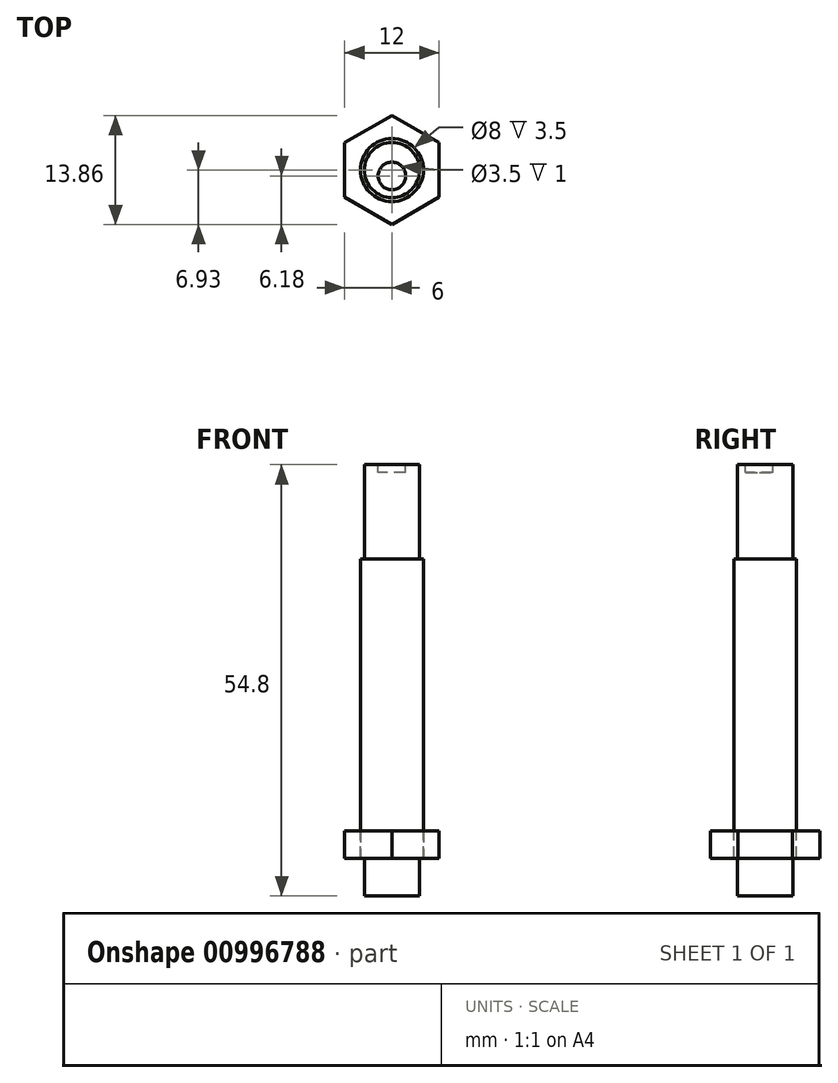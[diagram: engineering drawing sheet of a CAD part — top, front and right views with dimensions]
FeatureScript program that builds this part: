
annotation { "Feature Type Name" : "Feature", "Feature Type Description" : "" }
export const myFeature = defineFeature(function(context is Context, id is Id, definition is map)
    precondition{}
    {
        {
            var Q0;
            Q0=qCreatedBy(makeId("Front.planeOp"),FACE);
            var sketch = newSketch(context, id + "F0", { "sketchPlane" : qUnion([Q0])});
            skLineSegment(sketch, "E0.bottom", {"start": v(0, 0) * mm, "end": v(-4, 0) * mm});
            skLineSegment(sketch, "E0.top", {"start": v(0, 38) * mm, "end": v(-4, 38) * mm});
            skLineSegment(sketch, "E0.left", {"start": v(0, 0) * mm, "end": v(0, 38) * mm});
            skLineSegment(sketch, "E0.right", {"start": v(-4, 0) * mm, "end": v(-4, 38) * mm});
            skLineSegment(sketch, "E1.bottom", {"start": v(0, 0) * mm, "end": v(-3.5, 0) * mm});
            skLineSegment(sketch, "E1.top", {"start": v(0, -4.8) * mm, "end": v(-3.5, -4.8) * mm});
            skLineSegment(sketch, "E1.left", {"start": v(0, 0) * mm, "end": v(0, -4.8) * mm});
            skLineSegment(sketch, "E1.right", {"start": v(-3.5, 0) * mm, "end": v(-3.5, -4.8) * mm});
            skLineSegment(sketch, "E2.bottom", {"start": v(0, 38) * mm, "end": v(-3.5, 38) * mm});
            skLineSegment(sketch, "E2.top", {"start": v(0, 50) * mm, "end": v(-3.5, 50) * mm});
            skLineSegment(sketch, "E2.left", {"start": v(0, 38) * mm, "end": v(0, 50) * mm});
            skLineSegment(sketch, "E2.right", {"start": v(-3.5, 38) * mm, "end": v(-3.5, 50) * mm});
            skSolve(sketch);
        }
        {
            var Q0;
            {var subQ3=sQuery(id+"F0.wireOp",EDGE,"E0.left");Q0=makeQuery(id+"F0.imprint","IMPRINT",FACE,{"disambiguationData":[TD([[makeQuery(id+"F0.imprint","IMPRINT",EDGE,{"derivedFrom":subQ3}),1.0]])]});}
            var Q1;
            Q1=makeQuery(id+"F0.imprint","IMPRINT",FACE,{"disambiguationData":[TD([[makeQuery(id+"F0.imprint","IMPRINT",EDGE,{"derivedFrom":sQuery(id+"F0.wireOp",EDGE,"E1.top")}),-1.0]])]});
            var Q2;
            Q2=makeQuery(id+"F0.imprint","IMPRINT",FACE,{"disambiguationData":[TD([[makeQuery(id+"F0.imprint","IMPRINT",EDGE,{"derivedFrom":sQuery(id+"F0.wireOp",EDGE,"E2.top")}),1.0]])]});
            var Q3;
            Q3=sQuery(id+"F0.wireOp",EDGE,"E0.left");
            revolve(context, id + "F1", {"surfaceOperationType" : NewSurfaceOperationType.NEW, "entities" : qUnion([Q0, Q1, Q2]), "axis" : qUnion([Q3]), "revolveType" : RevolveType.FULL});
        }
        {
            var Q0;
            Q0=makeQuery(id+"F1.opRevolve","SWEPT_FACE",FACE,{"disambiguationData":[OSD([sQuery(id+"F0.wireOp",EDGE,"E2.top")])]});
            var sketch = newSketch(context, id + "F2", { "sketchPlane" : qUnion([Q0])});
            skLineSegment(sketch, "E3", {"start": v(0, 3.5) * mm, "end": v(0, -0.75) * mm, "construction": true});
            skCircle(sketch, "E4", {"center": v(0, -0.75) * mm, "radius": 1.75 * mm});
            skLineSegment(sketch, "E5", {"start": v(0, 0) * mm, "end": v(6, 0) * mm, "construction": true});
            skCircle(sketch, "E6.cCircle", {"center": v(0, 0) * mm, "radius": 6 * mm, "construction": true});
            skLineSegment(sketch, "E6.0", {"start": v(6, 3.46) * mm, "end": v(6, -3.46) * mm});
            skLineSegment(sketch, "E6.1", {"start": v(6, -3.46) * mm, "end": v(0, -6.93) * mm});
            skLineSegment(sketch, "E6.2", {"start": v(0, -6.93) * mm, "end": v(-6, -3.46) * mm});
            skLineSegment(sketch, "E6.3", {"start": v(-6, -3.46) * mm, "end": v(-6, 3.46) * mm});
            skLineSegment(sketch, "E6.4", {"start": v(-6, 3.46) * mm, "end": v(0, 6.93) * mm});
            skLineSegment(sketch, "E6.5", {"start": v(0, 6.93) * mm, "end": v(6, 3.46) * mm});
            skPoint(sketch, "E6.0.midPoint", {"position": v(6, 0) * mm});
            skCircle(sketch, "E7", {"center": v(0, 0) * mm, "radius": 4 * mm});
            skSolve(sketch);
        }
        {
            var Q0;
            Q0=makeQuery(id+"F2.imprint","IMPRINT",FACE,{"disambiguationData":[TD([[makeQuery(id+"F2.imprint","IMPRINT",EDGE,{"derivedFrom":sQuery(id+"F2.wireOp",EDGE,"E4")}),1.0]])]});
            extrude(context, id + "F3", {"entities" : qUnion([Q0]), "operationType" : NewBodyOperationType.REMOVE, "oppositeDirection" : true, "depth" : 1 * mm, "offsetDistance" : 25 * mm});
        }
        {
            var Q0;
            Q0=makeQuery(id+"F2.imprint","IMPRINT",FACE,{"disambiguationData":[TD([[makeQuery(id+"F2.imprint","IMPRINT",EDGE,{"derivedFrom":sQuery(id+"F2.wireOp",EDGE,"E6.0")}),-1.0]])]});
            extrude(context, id + "F4", {"entities" : qUnion([Q0]), "oppositeDirection" : true, "depth" : 50 * mm, "offsetDistance" : 25 * mm, "hasSecondDirection" : true, "secondDirectionOppositeDirection" : true, "secondDirectionDepth" : 46.5 * mm});
        }
    });
